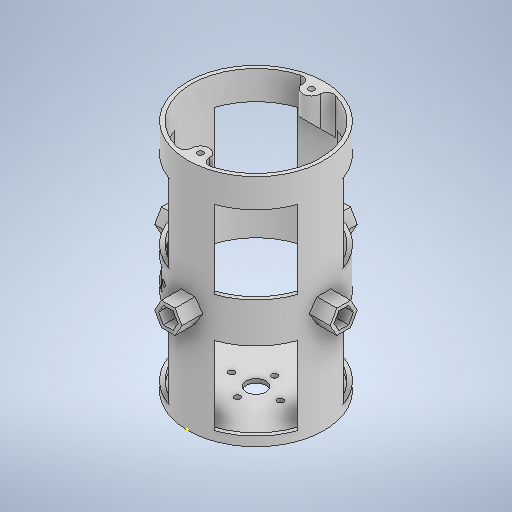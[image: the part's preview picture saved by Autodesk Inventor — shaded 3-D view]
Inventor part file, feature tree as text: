
AUTODESK INVENTOR PART (.ipt)
format: ipt  version: 2025.3 (Build 293356000, 356)  size: 532,480 bytes
history: native  units: in
note: dims shown in document units (in); Inventor stores cm internally (conversion verified against a paired STEP export)
features: sketch x9, extrude x8, mirror x5, fillet x4, plane x3, projected_geometry x2, shell x1, boolean_combine x1
ambient origin geometry x8: Origin, YZ Plane, XZ Plane, XY Plane, X Axis, Y Axis, Z Axis, Center Point
bodies: Solid1 (feature_tree), Solid2 (feature_tree)
feature tree (33):
  extrude  "Extrusion1"  Depth=0.0787in TaperAngle=0.0deg
  shell  "Shell1"  Thickness=0.0787in
  extrude  "Extrusion2"  Depth=0.1181in
  extrude  "Extrusion3"  Depth=0.3937in TaperAngle=0.0deg
  mirror  "Mirror2"
  boolean_combine  "Combine2"
  extrude  "Extrusion4"  Depth=0.122in
  plane  "Work Plane1"
  sketch  "Sketch7"  dims[d37=0.122in d38=0.122in]
  extrude  "Extrusion5"  Depth=0.122in
  plane  "Work Plane2"
  plane  "Work Plane3"
  extrude  "Extrusion7"  Depth=0.9843in
  fillet  "Face Fillet13"
  fillet  "Face Fillet14"
  fillet  "Face Fillet15"
  fillet  "Face Fillet16"
  extrude  "Extrusion10"  Depth=0.4921in
  extrude  "Extrusion9"  Depth=1.378in
  mirror  "Mirror5"
  mirror  "Mirror6"
  mirror  "Mirror7"
  mirror  "Mirror8"
  sketch  "Sketch1"  dims[d0=2.7559in d1=4.7244in d2=0.0in d3=0.0787in]
  sketch  "Sketch4"  dims[d15=0.3543in d16=0.1181in]
  sketch  "Sketch5"  dims[d17=0.7874in d18=0.0in d22=0.3937in d23=0.0in]
  sketch  "Sketch6"  dims[d35=0.122in d36=0.122in]
  sketch  "Sketch8"  dims[d39=0.748in d40=0.9843in]
  sketch  "Sketch10"  dims[d41=0.374in d42=0.4921in]
  sketch  "Sketch12"  dims[d43=0.3937in d44=0.0in d45=1.378in]
  projected_geometry  "Projected Loop5"
  projected_geometry  "Projected Loop6"
  sketch  "Sketch13"  dims[d46=2.1654in d49=0.3937in d50=0.0in d53=1.378in d54=0.4331in d55=0.6102in d56=0.1969in d57=0.1181in d58=0.0in d59=0.0in d60=45.0deg d61=0.1346in d62=0.1346in d63=0.1346in d64=0.1346in d65=0.3937in d66=0.5512in d67=2.1654in d68=2.1654in d69=1.5748in d71=45.0deg d72=0.3937in d73=0.3937in d76=0.3937in d77=0.0in d78=1.5748in d79=1.1811in d80=0.187in d81=1.5748in d82=1.1811in d83=0.187in d84=0.3937in d85=0.0in d74=0.0197in d75=0.0344in]
